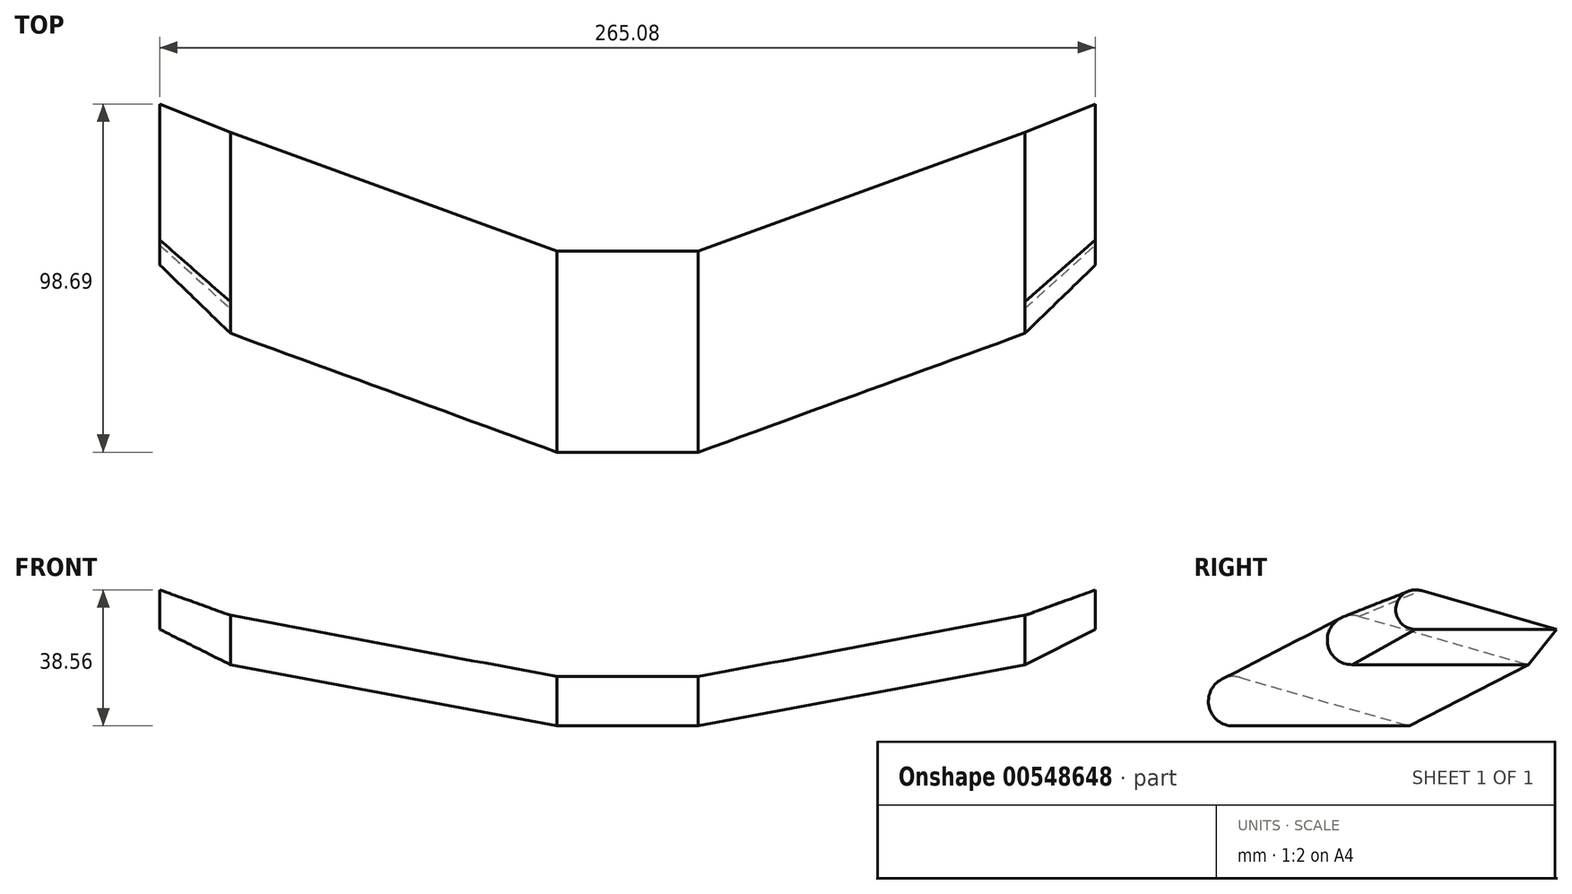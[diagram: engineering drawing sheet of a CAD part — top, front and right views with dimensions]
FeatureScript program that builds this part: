
annotation { "Feature Type Name" : "Feature", "Feature Type Description" : "" }
export const myFeature = defineFeature(function(context is Context, id is Id, definition is map)
    precondition{}
    {
        {
            var Q0;
            Q0=qCreatedBy(makeId("Right.planeOp"),FACE);
            var sketch = newSketch(context, id + "F0", { "sketchPlane" : qUnion([Q0])});
            skLineSegment(sketch, "E0", {"start": v(-85.82, 4.72) * mm, "end": v(-35.82, 4.72) * mm});
            skArc(sketch, "E1", {"start": v(-83.9, 18.45) * mm, "mid": v(-92.75, 12.69) * mm, "end": v(-85.82, 4.72) * mm});
            skLineSegment(sketch, "E2", {"start": v(-83.9, 18.45) * mm, "end": v(-35.82, 4.72) * mm});
            skSolve(sketch);
        }
        {
            var Q0;
            Q0=qCreatedBy(makeId("Top.planeOp"),FACE);
            var Q1;
            Q1=sQuery(id+"F0.wireOp",VERTEX,"E0.start");
            cPlane(context, id + "F1", {"entities" : qUnion([Q0, Q1]), "cplaneType" : CPlaneType.PLANE_POINT, "offset" : 25 * mm, "width" : 150 * mm, "height" : 150 * mm});
        }
        {
            var Q0;
            Q0=qCreatedBy(id+"F1.planeOp",FACE);
            var sketch = newSketch(context, id + "F2", { "sketchPlane" : qUnion([Q0])});
            skLineSegment(sketch, "E3", {"start": v(0, -85.82) * mm, "end": v(20, -85.82) * mm});
            skSolve(sketch);
        }
        {
            var Q0;
            Q0=qCreatedBy(makeId("Front.planeOp"),FACE);
            var Q1;
            Q1=sQuery(id+"F2.wireOp",VERTEX,"E3.end");
            cPlane(context, id + "F3", {"entities" : qUnion([Q0, Q1]), "cplaneType" : CPlaneType.PLANE_POINT, "offset" : 25 * mm, "width" : 150 * mm, "height" : 150 * mm});
        }
        {
            var Q0;
            Q0=qCreatedBy(id+"F3.planeOp",FACE);
            var sketch = newSketch(context, id + "F4", { "sketchPlane" : qUnion([Q0])});
            skLineSegment(sketch, "E4", {"start": v(20, 4.72) * mm, "end": v(20, 66.05) * mm});
            skSolve(sketch);
        }
        {
            var Q0;
            Q0=qCreatedBy(id+"F3.planeOp",FACE);
            var Q1;
            Q1=sQuery(id+"F4.wireOp",EDGE,"E4");
            cPlane(context, id + "F5", {"entities" : qUnion([Q0, Q1]), "cplaneType" : CPlaneType.LINE_ANGLE, "offset" : 25 * mm, "angle" : 20 * degree, "width" : 150 * mm, "height" : 150 * mm});
        }
        {
            var Q0;
            Q0=qCreatedBy(id+"F5.planeOp",FACE);
            var sketch = newSketch(context, id + "F6", { "sketchPlane" : qUnion([Q0])});
            skLineSegment(sketch, "E5", {"start": v(10.56, 4.72) * mm, "end": v(-87.92, 22.08) * mm});
            skSolve(sketch);
        }
        {
            var Q0;
            Q0=makeQuery(id+"F0.imprint","IMPRINT",FACE,{"disambiguationData":[TD([[makeQuery(id+"F0.imprint","IMPRINT",EDGE,{"derivedFrom":sQuery(id+"F0.wireOp",EDGE,"E0")}),1.0]])]});
            var Q1;
            Q1=sQuery(id+"F2.wireOp",EDGE,"E3");
            var Q2;
            Q2=sQuery(id+"F6.wireOp",EDGE,"E5");
            sweep(context, id + "F7", {"profiles" : qUnion([Q0]), "path" : qUnion([Q1, Q2]), "keepProfileOrientation" : true});
        }
        {
            var Q0;
            Q0=makeQuery(id+"F7.opSweep","CAP_FACE",FACE,{"disambiguationData":[OSD([sQuery(id+"F0.wireOp",EDGE,"E0"),sQuery(id+"F0.wireOp",EDGE,"E1"),sQuery(id+"F0.wireOp",EDGE,"E2"),sQuery(id+"F6.wireOp",VERTEX,"E5.end")])],"isStart":false});
            cPlane(context, id + "F8", {"entities" : qUnion([Q0]), "cplaneType" : CPlaneType.OFFSET, "offset" : 20 * mm, "width" : 150 * mm, "height" : 150 * mm});
        }
        {
            var Q0;
            Q0=qCreatedBy(id+"F8.planeOp",FACE);
            var sketch = newSketch(context, id + "F9", { "sketchPlane" : qUnion([Q0])});
            skLineSegment(sketch, "E6", {"start": v(-34.13, 32.08) * mm, "end": v(5.87, 32.08) * mm});
            skArc(sketch, "E7", {"start": v(-32.6, 43.07) * mm, "mid": v(-39.68, 38.46) * mm, "end": v(-34.13, 32.08) * mm});
            skLineSegment(sketch, "E8", {"start": v(-32.6, 43.07) * mm, "end": v(5.87, 32.08) * mm});
            skSolve(sketch);
        }
        {
            var Q1;
            Q1=makeQuery(id+"F7.opSweep","CAP_FACE",FACE,{"disambiguationData":[OSD([sQuery(id+"F0.wireOp",EDGE,"E0"),sQuery(id+"F0.wireOp",EDGE,"E1"),sQuery(id+"F0.wireOp",EDGE,"E2"),sQuery(id+"F6.wireOp",VERTEX,"E5.end")])],"isStart":false});
            var Q2;
            Q2=makeQuery(id+"F9.imprint","IMPRINT",FACE,{"disambiguationData":[TD([[makeQuery(id+"F9.imprint","IMPRINT",EDGE,{"derivedFrom":sQuery(id+"F9.wireOp",EDGE,"E6")}),1.0]])]});
            loft(context, id + "F10", {"operationType" : NewBodyOperationType.ADD, "sheetProfilesArray" : [{ "sheetProfileEntities" : qUnion([Q1]) }, { "sheetProfileEntities" : qUnion([Q2]) }]});
        }
        {
            var Q0;
            Q0=makeQuery(id+"F7.opSweep","SWEPT_BODY",BODY,{"disambiguationData":[OSD([sQuery(id+"F0.wireOp",EDGE,"E0"),sQuery(id+"F0.wireOp",EDGE,"E1"),sQuery(id+"F0.wireOp",EDGE,"E2"),sQuery(id+"F6.wireOp",EDGE,"E5")])]});
            var Q1;
            Q1=qCreatedBy(makeId("Right.planeOp"),FACE);
            mirror(context, id + "F11", {"operationType" : NewBodyOperationType.ADD, "entities" : qUnion([Q0]), "mirrorPlane" : qUnion([Q1])});
        }
    });
